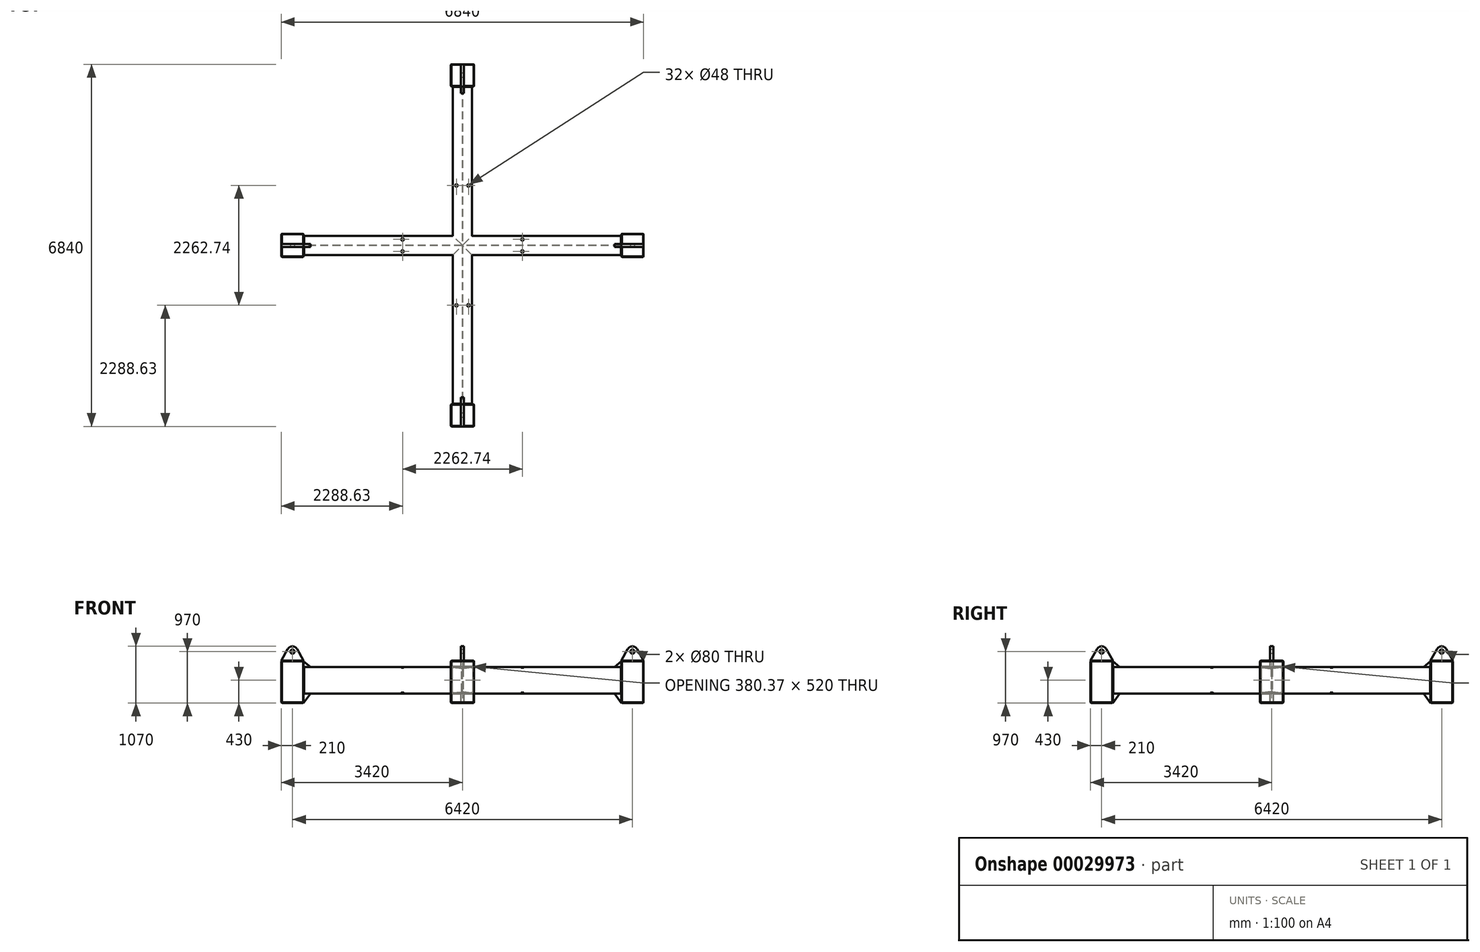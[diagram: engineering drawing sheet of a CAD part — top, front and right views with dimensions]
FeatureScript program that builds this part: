
annotation { "Feature Type Name" : "Feature", "Feature Type Description" : "" }
export const myFeature = defineFeature(function(context is Context, id is Id, definition is map)
    precondition{}
    {
        {
            var Q0;
            Q0=qCreatedBy(makeId("Front.planeOp"),FACE);
            var sketch = newSketch(context, id + "F0", { "sketchPlane" : qUnion([Q0])});
            skLineSegment(sketch, "E0", {"start": v(0, 886.2) * mm, "end": v(0, 0) * mm, "construction": true});
            skLineSegment(sketch, "E1", {"start": v(-180, 0) * mm, "end": v(180, 0) * mm});
            skLineSegment(sketch, "E2", {"start": v(180, 0) * mm, "end": v(180, -5.5) * mm});
            skLineSegment(sketch, "E3", {"start": v(180, -5.5) * mm, "end": v(4.95, -23.9) * mm});
            skLineSegment(sketch, "E4", {"start": v(4.95, -23.9) * mm, "end": v(4.95, -476.1) * mm});
            skLineSegment(sketch, "E5", {"start": v(4.95, -476.1) * mm, "end": v(180, -494.5) * mm});
            skLineSegment(sketch, "E6", {"start": v(180, -494.5) * mm, "end": v(180, -500) * mm});
            skLineSegment(sketch, "E7", {"start": v(180, -500) * mm, "end": v(-180, -500) * mm});
            skLineSegment(sketch, "E8", {"start": v(-180, -500) * mm, "end": v(-180, -494.5) * mm});
            skLineSegment(sketch, "E9", {"start": v(-180, -494.5) * mm, "end": v(-4.95, -476.1) * mm});
            skLineSegment(sketch, "E10", {"start": v(-4.95, -476.1) * mm, "end": v(-4.95, -23.9) * mm});
            skLineSegment(sketch, "E11", {"start": v(-4.95, -23.9) * mm, "end": v(-180, -5.5) * mm});
            skLineSegment(sketch, "E12", {"start": v(-180, -5.5) * mm, "end": v(-180, 0) * mm});
            skLineSegment(sketch, "E13", {"start": v(-180, -5.5) * mm, "end": v(-180, -494.5) * mm, "construction": true});
            skLineSegment(sketch, "E14", {"start": v(180, -5.5) * mm, "end": v(180, -494.5) * mm, "construction": true});
            skLineSegment(sketch, "E15", {"start": v(-4.95, -476.1) * mm, "end": v(4.95, -476.1) * mm, "construction": true});
            skLineSegment(sketch, "E16", {"start": v(-4.95, -23.9) * mm, "end": v(4.95, -23.9) * mm, "construction": true});
            skPoint(sketch, "E17", {"position": v(-92.48, -14.7) * mm});
            skLineSegment(sketch, "E18", {"start": v(-180, -250) * mm, "end": v(-341.33, -250) * mm, "construction": true});
            skSolve(sketch);
        }
        {
            var Q0;
            Q0 = qSketchRegion(id + "F0", true);
            extrude(context, id + "F1", {"entities" : qUnion([Q0]), "endBound" : BoundingType.SYMMETRIC, "depth" : 6000 * mm});
        }
        {
            var Q0;
            Q0=qCreatedBy(makeId("Right.planeOp"),FACE);
            var sketch = newSketch(context, id + "F2", { "sketchPlane" : qUnion([Q0])});
            skLineSegment(sketch, "E19", {"start": v(-180, -250) * mm, "end": v(-341.33, -250) * mm, "construction": true});
            skPoint(sketch, "E20", {"position": v(-92.47, -14.7) * mm});
            skLineSegment(sketch, "E21", {"start": v(-180, -5.5) * mm, "end": v(-180, -494.5) * mm, "construction": true});
            skLineSegment(sketch, "E22", {"start": v(180, -5.5) * mm, "end": v(180, -494.5) * mm, "construction": true});
            skLineSegment(sketch, "E23", {"start": v(0, 648.37) * mm, "end": v(0, -237.84) * mm, "construction": true});
            skLineSegment(sketch, "E24", {"start": v(-180, 0) * mm, "end": v(180, 0) * mm});
            skLineSegment(sketch, "E25", {"start": v(180, -500) * mm, "end": v(-180, -500) * mm});
            skLineSegment(sketch, "E26", {"start": v(180, -5.5) * mm, "end": v(4.95, -23.9) * mm});
            skLineSegment(sketch, "E27", {"start": v(4.95, -23.9) * mm, "end": v(4.95, -476.1) * mm});
            skLineSegment(sketch, "E28", {"start": v(-180, -494.5) * mm, "end": v(-4.95, -476.1) * mm});
            skLineSegment(sketch, "E29", {"start": v(4.95, -476.1) * mm, "end": v(180, -494.5) * mm});
            skLineSegment(sketch, "E30", {"start": v(-4.95, -476.1) * mm, "end": v(-4.95, -23.9) * mm});
            skLineSegment(sketch, "E31", {"start": v(-4.95, -23.9) * mm, "end": v(-180, -5.5) * mm});
            skLineSegment(sketch, "E32", {"start": v(-4.95, -476.1) * mm, "end": v(4.95, -476.1) * mm, "construction": true});
            skLineSegment(sketch, "E33", {"start": v(180, 0) * mm, "end": v(180, -5.5) * mm});
            skLineSegment(sketch, "E34", {"start": v(-180, -500) * mm, "end": v(-180, -494.5) * mm});
            skLineSegment(sketch, "E35", {"start": v(180, -494.5) * mm, "end": v(180, -500) * mm});
            skLineSegment(sketch, "E36", {"start": v(-180, -5.5) * mm, "end": v(-180, 0) * mm});
            skLineSegment(sketch, "E37", {"start": v(-4.95, -23.9) * mm, "end": v(4.95, -23.9) * mm, "construction": true});
            skLineSegment(sketch, "E38", {"start": v(0, 0) * mm, "end": v(0, 2027.1) * mm, "construction": true});
            skSolve(sketch);
        }
        {
            var Q0;
            Q0 = qSketchRegion(id + "F2", true);
            extrude(context, id + "F3", {"entities" : qUnion([Q0]), "operationType" : NewBodyOperationType.ADD, "endBound" : BoundingType.SYMMETRIC, "depth" : 6000 * mm});
        }
        {
            var Q0;
            {var subQ0=sQuery(id+"F0.wireOp",EDGE,"E4");var subQ1=sQuery(id+"F0.wireOp",EDGE,"E5");Q0=makeQuery(id+"F3.boolean.opBoolean","SPLIT",EDGE,{"disambiguationData":[TD([makeQuery(id+"F3.opExtrude","SWEPT_FACE",FACE,{"disambiguationData":[OSD([sQuery(id+"F2.wireOp",EDGE,"E28")])]})])],"derivedFrom":makeQuery(id+"F1.opExtrude","SWEPT_EDGE",EDGE,{"disambiguationData":[OSD([subQ0,subQ1])]})});}
            var Q1;
            {var subQ0=sQuery(id+"F0.wireOp",EDGE,"E9");var subQ1=sQuery(id+"F0.wireOp",EDGE,"E10");Q1=makeQuery(id+"F3.boolean.opBoolean","SPLIT",EDGE,{"disambiguationData":[TD([makeQuery(id+"F3.opExtrude","SWEPT_FACE",FACE,{"disambiguationData":[OSD([sQuery(id+"F2.wireOp",EDGE,"E28")])]})])],"derivedFrom":makeQuery(id+"F1.opExtrude","SWEPT_EDGE",EDGE,{"disambiguationData":[OSD([subQ0,subQ1])]})});}
            var Q2;
            {var subQ0=sQuery(id+"F0.wireOp",EDGE,"E10");var subQ1=sQuery(id+"F0.wireOp",EDGE,"E11");Q2=makeQuery(id+"F3.boolean.opBoolean","SPLIT",EDGE,{"disambiguationData":[TD([makeQuery(id+"F3.opExtrude","SWEPT_FACE",FACE,{"disambiguationData":[OSD([sQuery(id+"F2.wireOp",EDGE,"E30")])]})])],"derivedFrom":makeQuery(id+"F1.opExtrude","SWEPT_EDGE",EDGE,{"disambiguationData":[OSD([subQ0,subQ1])]})});}
            var Q3;
            {var subQ0=sQuery(id+"F0.wireOp",EDGE,"E3");var subQ1=sQuery(id+"F0.wireOp",EDGE,"E4");Q3=makeQuery(id+"F3.boolean.opBoolean","SPLIT",EDGE,{"disambiguationData":[TD([makeQuery(id+"F3.opExtrude","SWEPT_FACE",FACE,{"disambiguationData":[OSD([sQuery(id+"F2.wireOp",EDGE,"E30")])]})])],"derivedFrom":makeQuery(id+"F1.opExtrude","SWEPT_EDGE",EDGE,{"disambiguationData":[OSD([subQ0,subQ1])]})});}
            var Q4;
            {var subQ0=sQuery(id+"F2.wireOp",EDGE,"E30");var subQ1=sQuery(id+"F2.wireOp",EDGE,"E31");Q4=makeQuery(id+"F3.boolean.opBoolean","SPLIT",EDGE,{"disambiguationData":[TD([makeQuery(id+"F1.opExtrude","SWEPT_FACE",FACE,{"disambiguationData":[OSD([sQuery(id+"F0.wireOp",EDGE,"E3")])]})])],"derivedFrom":makeQuery(id+"F3.opExtrude","SWEPT_EDGE",EDGE,{"disambiguationData":[OSD([subQ0,subQ1])]})});}
            var Q5;
            {var subQ0=sQuery(id+"F2.wireOp",EDGE,"E28");var subQ1=sQuery(id+"F2.wireOp",EDGE,"E30");Q5=makeQuery(id+"F3.boolean.opBoolean","SPLIT",EDGE,{"disambiguationData":[TD([makeQuery(id+"F1.opExtrude","SWEPT_FACE",FACE,{"disambiguationData":[OSD([sQuery(id+"F0.wireOp",EDGE,"E4")])]})])],"derivedFrom":makeQuery(id+"F3.opExtrude","SWEPT_EDGE",EDGE,{"disambiguationData":[OSD([subQ0,subQ1])]})});}
            var Q6;
            {var subQ0=sQuery(id+"F2.wireOp",EDGE,"E27");var subQ1=sQuery(id+"F2.wireOp",EDGE,"E29");Q6=makeQuery(id+"F3.boolean.opBoolean","SPLIT",EDGE,{"disambiguationData":[TD([makeQuery(id+"F1.opExtrude","SWEPT_FACE",FACE,{"disambiguationData":[OSD([sQuery(id+"F0.wireOp",EDGE,"E4")])]})])],"derivedFrom":makeQuery(id+"F3.opExtrude","SWEPT_EDGE",EDGE,{"disambiguationData":[OSD([subQ0,subQ1])]})});}
            var Q7;
            {var subQ0=sQuery(id+"F2.wireOp",EDGE,"E26");var subQ1=sQuery(id+"F2.wireOp",EDGE,"E27");Q7=makeQuery(id+"F3.boolean.opBoolean","SPLIT",EDGE,{"disambiguationData":[TD([makeQuery(id+"F1.opExtrude","SWEPT_FACE",FACE,{"disambiguationData":[OSD([sQuery(id+"F0.wireOp",EDGE,"E3")])]})])],"derivedFrom":makeQuery(id+"F3.opExtrude","SWEPT_EDGE",EDGE,{"disambiguationData":[OSD([subQ0,subQ1])]})});}
            var Q8;
            {var subQ0=sQuery(id+"F0.wireOp",EDGE,"E4");var subQ1=sQuery(id+"F0.wireOp",EDGE,"E5");Q8=makeQuery(id+"F3.boolean.opBoolean","SPLIT",EDGE,{"disambiguationData":[TD([makeQuery(id+"F3.opExtrude","SWEPT_FACE",FACE,{"disambiguationData":[OSD([sQuery(id+"F2.wireOp",EDGE,"E27")])]})])],"derivedFrom":makeQuery(id+"F1.opExtrude","SWEPT_EDGE",EDGE,{"disambiguationData":[OSD([subQ0,subQ1])]})});}
            var Q9;
            {var subQ0=sQuery(id+"F0.wireOp",EDGE,"E3");var subQ1=sQuery(id+"F0.wireOp",EDGE,"E4");Q9=makeQuery(id+"F3.boolean.opBoolean","SPLIT",EDGE,{"disambiguationData":[TD([makeQuery(id+"F3.opExtrude","SWEPT_FACE",FACE,{"disambiguationData":[OSD([sQuery(id+"F2.wireOp",EDGE,"E26")])]})])],"derivedFrom":makeQuery(id+"F1.opExtrude","SWEPT_EDGE",EDGE,{"disambiguationData":[OSD([subQ0,subQ1])]})});}
            var Q10;
            {var subQ0=sQuery(id+"F0.wireOp",EDGE,"E9");var subQ1=sQuery(id+"F0.wireOp",EDGE,"E10");Q10=makeQuery(id+"F3.boolean.opBoolean","SPLIT",EDGE,{"disambiguationData":[TD([makeQuery(id+"F3.opExtrude","SWEPT_FACE",FACE,{"disambiguationData":[OSD([sQuery(id+"F2.wireOp",EDGE,"E27")])]})])],"derivedFrom":makeQuery(id+"F1.opExtrude","SWEPT_EDGE",EDGE,{"disambiguationData":[OSD([subQ0,subQ1])]})});}
            var Q11;
            {var subQ0=sQuery(id+"F0.wireOp",EDGE,"E10");var subQ1=sQuery(id+"F0.wireOp",EDGE,"E11");Q11=makeQuery(id+"F3.boolean.opBoolean","SPLIT",EDGE,{"disambiguationData":[TD([makeQuery(id+"F3.opExtrude","SWEPT_FACE",FACE,{"disambiguationData":[OSD([sQuery(id+"F2.wireOp",EDGE,"E26")])]})])],"derivedFrom":makeQuery(id+"F1.opExtrude","SWEPT_EDGE",EDGE,{"disambiguationData":[OSD([subQ0,subQ1])]})});}
            var Q12;
            {var subQ0=sQuery(id+"F2.wireOp",EDGE,"E27");var subQ1=sQuery(id+"F2.wireOp",EDGE,"E29");Q12=makeQuery(id+"F3.boolean.opBoolean","SPLIT",EDGE,{"disambiguationData":[TD([makeQuery(id+"F1.opExtrude","SWEPT_FACE",FACE,{"disambiguationData":[OSD([sQuery(id+"F0.wireOp",EDGE,"E9")])]})])],"derivedFrom":makeQuery(id+"F3.opExtrude","SWEPT_EDGE",EDGE,{"disambiguationData":[OSD([subQ0,subQ1])]})});}
            var Q13;
            {var subQ0=sQuery(id+"F2.wireOp",EDGE,"E26");var subQ1=sQuery(id+"F2.wireOp",EDGE,"E27");Q13=makeQuery(id+"F3.boolean.opBoolean","SPLIT",EDGE,{"disambiguationData":[TD([makeQuery(id+"F1.opExtrude","SWEPT_FACE",FACE,{"disambiguationData":[OSD([sQuery(id+"F0.wireOp",EDGE,"E10")])]})])],"derivedFrom":makeQuery(id+"F3.opExtrude","SWEPT_EDGE",EDGE,{"disambiguationData":[OSD([subQ0,subQ1])]})});}
            var Q14;
            {var subQ0=sQuery(id+"F2.wireOp",EDGE,"E28");var subQ1=sQuery(id+"F2.wireOp",EDGE,"E30");Q14=makeQuery(id+"F3.boolean.opBoolean","SPLIT",EDGE,{"disambiguationData":[TD([makeQuery(id+"F1.opExtrude","SWEPT_FACE",FACE,{"disambiguationData":[OSD([sQuery(id+"F0.wireOp",EDGE,"E9")])]})])],"derivedFrom":makeQuery(id+"F3.opExtrude","SWEPT_EDGE",EDGE,{"disambiguationData":[OSD([subQ0,subQ1])]})});}
            var Q15;
            {var subQ0=sQuery(id+"F2.wireOp",EDGE,"E30");var subQ1=sQuery(id+"F2.wireOp",EDGE,"E31");Q15=makeQuery(id+"F3.boolean.opBoolean","SPLIT",EDGE,{"disambiguationData":[TD([makeQuery(id+"F1.opExtrude","SWEPT_FACE",FACE,{"disambiguationData":[OSD([sQuery(id+"F0.wireOp",EDGE,"E10")])]})])],"derivedFrom":makeQuery(id+"F3.opExtrude","SWEPT_EDGE",EDGE,{"disambiguationData":[OSD([subQ0,subQ1])]})});}
            fillet(context, id + "F4", {"entities" : qUnion([Q0, Q1, Q2, Q3, Q4, Q5, Q6, Q7, Q8, Q9, Q10, Q11, Q12, Q13, Q14, Q15]), "radius" : 16 * mm, "tangentPropagation" : true, "allowEdgeOverflow" : false});
        }
        {
            var Q0;
            {var subQ0=sQuery(id+"F0.wireOp",EDGE,"E5");var subQ1=sQuery(id+"F0.wireOp",EDGE,"E6");Q0=makeQuery(id+"F3.boolean.opBoolean","SPLIT",EDGE,{"disambiguationData":[TD([makeQuery(id+"F3.opExtrude","SWEPT_FACE",FACE,{"disambiguationData":[OSD([sQuery(id+"F2.wireOp",EDGE,"E28")])]})])],"derivedFrom":makeQuery(id+"F1.opExtrude","SWEPT_EDGE",EDGE,{"disambiguationData":[OSD([subQ0,subQ1])]})});}
            var Q1;
            {var subQ0=sQuery(id+"F0.wireOp",EDGE,"E2");var subQ1=sQuery(id+"F0.wireOp",EDGE,"E3");Q1=makeQuery(id+"F3.boolean.opBoolean","SPLIT",EDGE,{"disambiguationData":[TD([makeQuery(id+"F3.opExtrude","SWEPT_FACE",FACE,{"disambiguationData":[OSD([sQuery(id+"F2.wireOp",EDGE,"E31")])]})])],"derivedFrom":makeQuery(id+"F1.opExtrude","SWEPT_EDGE",EDGE,{"disambiguationData":[OSD([subQ0,subQ1])]})});}
            var Q2;
            {var subQ0=sQuery(id+"F0.wireOp",EDGE,"E8");var subQ1=sQuery(id+"F0.wireOp",EDGE,"E9");Q2=makeQuery(id+"F3.boolean.opBoolean","SPLIT",EDGE,{"disambiguationData":[TD([makeQuery(id+"F3.opExtrude","SWEPT_FACE",FACE,{"disambiguationData":[OSD([sQuery(id+"F2.wireOp",EDGE,"E28")])]})])],"derivedFrom":makeQuery(id+"F1.opExtrude","SWEPT_EDGE",EDGE,{"disambiguationData":[OSD([subQ0,subQ1])]})});}
            var Q3;
            {var subQ0=sQuery(id+"F0.wireOp",EDGE,"E11");var subQ1=sQuery(id+"F0.wireOp",EDGE,"E12");Q3=makeQuery(id+"F3.boolean.opBoolean","SPLIT",EDGE,{"disambiguationData":[TD([makeQuery(id+"F3.opExtrude","SWEPT_FACE",FACE,{"disambiguationData":[OSD([sQuery(id+"F2.wireOp",EDGE,"E31")])]})])],"derivedFrom":makeQuery(id+"F1.opExtrude","SWEPT_EDGE",EDGE,{"disambiguationData":[OSD([subQ0,subQ1])]})});}
            var Q4;
            {var subQ0=sQuery(id+"F2.wireOp",EDGE,"E28");var subQ1=sQuery(id+"F2.wireOp",EDGE,"E34");Q4=makeQuery(id+"F3.boolean.opBoolean","SPLIT",EDGE,{"disambiguationData":[TD([makeQuery(id+"F1.opExtrude","SWEPT_FACE",FACE,{"disambiguationData":[OSD([sQuery(id+"F0.wireOp",EDGE,"E8")])]})])],"derivedFrom":makeQuery(id+"F3.opExtrude","SWEPT_EDGE",EDGE,{"disambiguationData":[OSD([subQ0,subQ1])]})});}
            var Q5;
            {var subQ0=sQuery(id+"F2.wireOp",EDGE,"E31");var subQ1=sQuery(id+"F2.wireOp",EDGE,"E36");Q5=makeQuery(id+"F3.boolean.opBoolean","SPLIT",EDGE,{"disambiguationData":[TD([makeQuery(id+"F1.opExtrude","SWEPT_FACE",FACE,{"disambiguationData":[OSD([sQuery(id+"F0.wireOp",EDGE,"E11")])]})])],"derivedFrom":makeQuery(id+"F3.opExtrude","SWEPT_EDGE",EDGE,{"disambiguationData":[OSD([subQ0,subQ1])]})});}
            var Q6;
            {var subQ0=sQuery(id+"F2.wireOp",EDGE,"E28");var subQ1=sQuery(id+"F2.wireOp",EDGE,"E34");Q6=makeQuery(id+"F3.boolean.opBoolean","SPLIT",EDGE,{"disambiguationData":[TD([makeQuery(id+"F1.opExtrude","SWEPT_FACE",FACE,{"disambiguationData":[OSD([sQuery(id+"F0.wireOp",EDGE,"E5")])]})])],"derivedFrom":makeQuery(id+"F3.opExtrude","SWEPT_EDGE",EDGE,{"disambiguationData":[OSD([subQ0,subQ1])]})});}
            var Q7;
            {var subQ0=sQuery(id+"F2.wireOp",EDGE,"E31");var subQ1=sQuery(id+"F2.wireOp",EDGE,"E36");Q7=makeQuery(id+"F3.boolean.opBoolean","SPLIT",EDGE,{"disambiguationData":[TD([makeQuery(id+"F1.opExtrude","SWEPT_FACE",FACE,{"disambiguationData":[OSD([sQuery(id+"F0.wireOp",EDGE,"E2")])]})])],"derivedFrom":makeQuery(id+"F3.opExtrude","SWEPT_EDGE",EDGE,{"disambiguationData":[OSD([subQ0,subQ1])]})});}
            var Q8;
            {var subQ0=sQuery(id+"F2.wireOp",EDGE,"E29");var subQ1=sQuery(id+"F2.wireOp",EDGE,"E35");Q8=makeQuery(id+"F3.boolean.opBoolean","SPLIT",EDGE,{"disambiguationData":[TD([makeQuery(id+"F1.opExtrude","SWEPT_FACE",FACE,{"disambiguationData":[OSD([sQuery(id+"F0.wireOp",EDGE,"E5")])]})])],"derivedFrom":makeQuery(id+"F3.opExtrude","SWEPT_EDGE",EDGE,{"disambiguationData":[OSD([subQ0,subQ1])]})});}
            var Q9;
            {var subQ0=sQuery(id+"F2.wireOp",EDGE,"E26");var subQ1=sQuery(id+"F2.wireOp",EDGE,"E33");Q9=makeQuery(id+"F3.boolean.opBoolean","SPLIT",EDGE,{"disambiguationData":[TD([makeQuery(id+"F1.opExtrude","SWEPT_FACE",FACE,{"disambiguationData":[OSD([sQuery(id+"F0.wireOp",EDGE,"E2")])]})])],"derivedFrom":makeQuery(id+"F3.opExtrude","SWEPT_EDGE",EDGE,{"disambiguationData":[OSD([subQ0,subQ1])]})});}
            var Q10;
            {var subQ0=sQuery(id+"F0.wireOp",EDGE,"E2");var subQ1=sQuery(id+"F0.wireOp",EDGE,"E3");Q10=makeQuery(id+"F3.boolean.opBoolean","SPLIT",EDGE,{"disambiguationData":[TD([makeQuery(id+"F3.opExtrude","SWEPT_FACE",FACE,{"disambiguationData":[OSD([sQuery(id+"F2.wireOp",EDGE,"E26")])]})])],"derivedFrom":makeQuery(id+"F1.opExtrude","SWEPT_EDGE",EDGE,{"disambiguationData":[OSD([subQ0,subQ1])]})});}
            var Q11;
            {var subQ0=sQuery(id+"F0.wireOp",EDGE,"E5");var subQ1=sQuery(id+"F0.wireOp",EDGE,"E6");Q11=makeQuery(id+"F3.boolean.opBoolean","SPLIT",EDGE,{"disambiguationData":[TD([makeQuery(id+"F3.opExtrude","SWEPT_FACE",FACE,{"disambiguationData":[OSD([sQuery(id+"F2.wireOp",EDGE,"E29")])]})])],"derivedFrom":makeQuery(id+"F1.opExtrude","SWEPT_EDGE",EDGE,{"disambiguationData":[OSD([subQ0,subQ1])]})});}
            var Q12;
            {var subQ0=sQuery(id+"F0.wireOp",EDGE,"E8");var subQ1=sQuery(id+"F0.wireOp",EDGE,"E9");Q12=makeQuery(id+"F3.boolean.opBoolean","SPLIT",EDGE,{"disambiguationData":[TD([makeQuery(id+"F3.opExtrude","SWEPT_FACE",FACE,{"disambiguationData":[OSD([sQuery(id+"F2.wireOp",EDGE,"E29")])]})])],"derivedFrom":makeQuery(id+"F1.opExtrude","SWEPT_EDGE",EDGE,{"disambiguationData":[OSD([subQ0,subQ1])]})});}
            var Q13;
            {var subQ0=sQuery(id+"F0.wireOp",EDGE,"E11");var subQ1=sQuery(id+"F0.wireOp",EDGE,"E12");Q13=makeQuery(id+"F3.boolean.opBoolean","SPLIT",EDGE,{"disambiguationData":[TD([makeQuery(id+"F3.opExtrude","SWEPT_FACE",FACE,{"disambiguationData":[OSD([sQuery(id+"F2.wireOp",EDGE,"E26")])]})])],"derivedFrom":makeQuery(id+"F1.opExtrude","SWEPT_EDGE",EDGE,{"disambiguationData":[OSD([subQ0,subQ1])]})});}
            var Q14;
            {var subQ0=sQuery(id+"F2.wireOp",EDGE,"E26");var subQ1=sQuery(id+"F2.wireOp",EDGE,"E33");Q14=makeQuery(id+"F3.boolean.opBoolean","SPLIT",EDGE,{"disambiguationData":[TD([makeQuery(id+"F1.opExtrude","SWEPT_FACE",FACE,{"disambiguationData":[OSD([sQuery(id+"F0.wireOp",EDGE,"E11")])]})])],"derivedFrom":makeQuery(id+"F3.opExtrude","SWEPT_EDGE",EDGE,{"disambiguationData":[OSD([subQ0,subQ1])]})});}
            var Q15;
            {var subQ0=sQuery(id+"F2.wireOp",EDGE,"E29");var subQ1=sQuery(id+"F2.wireOp",EDGE,"E35");Q15=makeQuery(id+"F3.boolean.opBoolean","SPLIT",EDGE,{"disambiguationData":[TD([makeQuery(id+"F1.opExtrude","SWEPT_FACE",FACE,{"disambiguationData":[OSD([sQuery(id+"F0.wireOp",EDGE,"E8")])]})])],"derivedFrom":makeQuery(id+"F3.opExtrude","SWEPT_EDGE",EDGE,{"disambiguationData":[OSD([subQ0,subQ1])]})});}
            fillet(context, id + "F5", {"entities" : qUnion([Q0, Q1, Q2, Q3, Q4, Q5, Q6, Q7, Q8, Q9, Q10, Q11, Q12, Q13, Q14, Q15]), "radius" : 8 * mm, "tangentPropagation" : true, "allowEdgeOverflow" : false});
        }
        {
            var Q0;
            Q0=makeQuery(id+"F3.boolean.opBoolean","MERGE",FACE,{"derivedFrom":[makeQuery(id+"F1.opExtrude","SWEPT_FACE",FACE,{"disambiguationData":[OSD([sQuery(id+"F0.wireOp",EDGE,"E1")])]}),makeQuery(id+"F3.opExtrude","SWEPT_FACE",FACE,{"disambiguationData":[OSD([sQuery(id+"F2.wireOp",EDGE,"E24")])]})]});
            var sketch = newSketch(context, id + "F6", { "sketchPlane" : qUnion([Q0])});
            skLineSegment(sketch, "E39", {"start": v(0, 0) * mm, "end": v(4594.2, 0) * mm, "construction": true});
            skLineSegment(sketch, "E40.bottom", {"start": v(3000, 220) * mm, "end": v(3420, 220) * mm});
            skLineSegment(sketch, "E40.top", {"start": v(3000, -220) * mm, "end": v(3420, -220) * mm});
            skLineSegment(sketch, "E40.left", {"start": v(3000, 220) * mm, "end": v(3000, -220) * mm});
            skLineSegment(sketch, "E40.right", {"start": v(3420, 220) * mm, "end": v(3420, -220) * mm});
            skLineSegment(sketch, "E41", {"start": v(0, 0) * mm, "end": v(0, 3976.5) * mm, "construction": true});
            skLineSegment(sketch, "E42.MirrorCS", {"start": v(-3000, -220) * mm, "end": v(-3420, -220) * mm});
            skLineSegment(sketch, "E43.MirrorCS", {"start": v(-3420, 220) * mm, "end": v(-3420, -220) * mm});
            skLineSegment(sketch, "E44.MirrorCS", {"start": v(-3000, 220) * mm, "end": v(-3000, -220) * mm});
            skLineSegment(sketch, "E45.MirrorCS", {"start": v(-3000, 220) * mm, "end": v(-3420, 220) * mm});
            skLineSegment(sketch, "E46.bottom", {"start": v(-220, 3420) * mm, "end": v(220, 3420) * mm});
            skLineSegment(sketch, "E46.top", {"start": v(-220, 3000) * mm, "end": v(220, 3000) * mm});
            skLineSegment(sketch, "E46.left", {"start": v(-220, 3420) * mm, "end": v(-220, 3000) * mm});
            skLineSegment(sketch, "E46.right", {"start": v(220, 3420) * mm, "end": v(220, 3000) * mm});
            skLineSegment(sketch, "E47.MirrorCS", {"start": v(220, -3420) * mm, "end": v(220, -3000) * mm});
            skLineSegment(sketch, "E48.MirrorCS", {"start": v(-220, -3420) * mm, "end": v(220, -3420) * mm});
            skLineSegment(sketch, "E49.MirrorCS", {"start": v(-220, -3000) * mm, "end": v(220, -3000) * mm});
            skLineSegment(sketch, "E50.MirrorCS", {"start": v(-220, -3420) * mm, "end": v(-220, -3000) * mm});
            skSolve(sketch);
        }
        {
            var Q0;
            Q0 = qSketchRegion(id + "F6", true);
            extrude(context, id + "F7", {"entities" : qUnion([Q0]), "operationType" : NewBodyOperationType.ADD, "depth" : 120 * mm, "hasSecondDirection" : true, "secondDirectionOppositeDirection" : true, "secondDirectionDepth" : (800 - 120) * mm});
        }
        {
            var Q0;
            Q0=makeQuery(id+"F7.opExtrude","SWEPT_FACE",FACE,{"disambiguationData":[OSD([sQuery(id+"F6.wireOp",EDGE,"E40.top")])]});
            var Q1;
            Q1=makeQuery(id+"F7.opExtrude","SWEPT_FACE",FACE,{"disambiguationData":[OSD([sQuery(id+"F6.wireOp",EDGE,"E40.right")])]});
            var Q2;
            Q2=makeQuery(id+"F7.opExtrude","CAP_FACE",FACE,{"disambiguationData":[OSD([sQuery(id+"F6.wireOp",EDGE,"E40.bottom"),sQuery(id+"F6.wireOp",EDGE,"E40.top"),sQuery(id+"F6.wireOp",EDGE,"E40.left"),sQuery(id+"F6.wireOp",EDGE,"E40.right")])],"isStart":false});
            var Q3;
            Q3=makeQuery(id+"F7.opExtrude","SWEPT_FACE",FACE,{"disambiguationData":[OSD([sQuery(id+"F6.wireOp",EDGE,"E40.bottom")])]});
            var Q4;
            Q4=makeQuery(id+"F7.opExtrude","CAP_FACE",FACE,{"disambiguationData":[OSD([sQuery(id+"F6.wireOp",EDGE,"E40.bottom"),sQuery(id+"F6.wireOp",EDGE,"E40.top"),sQuery(id+"F6.wireOp",EDGE,"E40.left"),sQuery(id+"F6.wireOp",EDGE,"E40.right")])],"isStart":true});
            var Q5;
            Q5=makeQuery(id+"F7.opExtrude","SWEPT_FACE",FACE,{"disambiguationData":[OSD([sQuery(id+"F6.wireOp",EDGE,"E40.left")])]});
            var Q6;
            Q6=makeQuery(id+"F7.opExtrude","SWEPT_FACE",FACE,{"disambiguationData":[OSD([sQuery(id+"F6.wireOp",EDGE,"E48.MirrorCS")])]});
            var Q7;
            Q7=makeQuery(id+"F7.opExtrude","SWEPT_FACE",FACE,{"disambiguationData":[OSD([sQuery(id+"F6.wireOp",EDGE,"E47.MirrorCS")])]});
            var Q8;
            Q8=makeQuery(id+"F7.opExtrude","CAP_FACE",FACE,{"disambiguationData":[OSD([sQuery(id+"F6.wireOp",EDGE,"E47.MirrorCS"),sQuery(id+"F6.wireOp",EDGE,"E48.MirrorCS"),sQuery(id+"F6.wireOp",EDGE,"E49.MirrorCS"),sQuery(id+"F6.wireOp",EDGE,"E50.MirrorCS")])],"isStart":false});
            var Q9;
            Q9=makeQuery(id+"F7.opExtrude","SWEPT_FACE",FACE,{"disambiguationData":[OSD([sQuery(id+"F6.wireOp",EDGE,"E50.MirrorCS")])]});
            var Q10;
            Q10=makeQuery(id+"F7.opExtrude","CAP_FACE",FACE,{"disambiguationData":[OSD([sQuery(id+"F6.wireOp",EDGE,"E47.MirrorCS"),sQuery(id+"F6.wireOp",EDGE,"E48.MirrorCS"),sQuery(id+"F6.wireOp",EDGE,"E49.MirrorCS"),sQuery(id+"F6.wireOp",EDGE,"E50.MirrorCS")])],"isStart":true});
            var Q11;
            Q11=makeQuery(id+"F7.opExtrude","SWEPT_FACE",FACE,{"disambiguationData":[OSD([sQuery(id+"F6.wireOp",EDGE,"E49.MirrorCS")])]});
            var Q12;
            Q12=makeQuery(id+"F7.opExtrude","SWEPT_FACE",FACE,{"disambiguationData":[OSD([sQuery(id+"F6.wireOp",EDGE,"E45.MirrorCS")])]});
            var Q13;
            Q13=makeQuery(id+"F7.opExtrude","CAP_FACE",FACE,{"disambiguationData":[OSD([sQuery(id+"F6.wireOp",EDGE,"E42.MirrorCS"),sQuery(id+"F6.wireOp",EDGE,"E43.MirrorCS"),sQuery(id+"F6.wireOp",EDGE,"E44.MirrorCS"),sQuery(id+"F6.wireOp",EDGE,"E45.MirrorCS")])],"isStart":true});
            var Q14;
            Q14=makeQuery(id+"F7.opExtrude","SWEPT_FACE",FACE,{"disambiguationData":[OSD([sQuery(id+"F6.wireOp",EDGE,"E43.MirrorCS")])]});
            var Q15;
            Q15=makeQuery(id+"F7.opExtrude","SWEPT_FACE",FACE,{"disambiguationData":[OSD([sQuery(id+"F6.wireOp",EDGE,"E42.MirrorCS")])]});
            var Q16;
            Q16=makeQuery(id+"F7.opExtrude","CAP_FACE",FACE,{"disambiguationData":[OSD([sQuery(id+"F6.wireOp",EDGE,"E42.MirrorCS"),sQuery(id+"F6.wireOp",EDGE,"E43.MirrorCS"),sQuery(id+"F6.wireOp",EDGE,"E44.MirrorCS"),sQuery(id+"F6.wireOp",EDGE,"E45.MirrorCS")])],"isStart":false});
            var Q17;
            Q17=makeQuery(id+"F7.opExtrude","SWEPT_FACE",FACE,{"disambiguationData":[OSD([sQuery(id+"F6.wireOp",EDGE,"E44.MirrorCS")])]});
            var Q18;
            Q18=makeQuery(id+"F7.opExtrude","SWEPT_FACE",FACE,{"disambiguationData":[OSD([sQuery(id+"F6.wireOp",EDGE,"E46.left")])]});
            var Q19;
            Q19=makeQuery(id+"F7.opExtrude","SWEPT_FACE",FACE,{"disambiguationData":[OSD([sQuery(id+"F6.wireOp",EDGE,"E46.top")])]});
            var Q20;
            Q20=makeQuery(id+"F7.opExtrude","CAP_FACE",FACE,{"disambiguationData":[OSD([sQuery(id+"F6.wireOp",EDGE,"E46.bottom"),sQuery(id+"F6.wireOp",EDGE,"E46.top"),sQuery(id+"F6.wireOp",EDGE,"E46.left"),sQuery(id+"F6.wireOp",EDGE,"E46.right")])],"isStart":false});
            var Q21;
            Q21=makeQuery(id+"F7.opExtrude","SWEPT_FACE",FACE,{"disambiguationData":[OSD([sQuery(id+"F6.wireOp",EDGE,"E46.bottom")])]});
            var Q22;
            Q22=makeQuery(id+"F7.opExtrude","SWEPT_FACE",FACE,{"disambiguationData":[OSD([sQuery(id+"F6.wireOp",EDGE,"E46.right")])]});
            var Q23;
            Q23=makeQuery(id+"F7.opExtrude","CAP_FACE",FACE,{"disambiguationData":[OSD([sQuery(id+"F6.wireOp",EDGE,"E46.bottom"),sQuery(id+"F6.wireOp",EDGE,"E46.top"),sQuery(id+"F6.wireOp",EDGE,"E46.left"),sQuery(id+"F6.wireOp",EDGE,"E46.right")])],"isStart":true});
            chamfer(context, id + "F8", {"entities" : qUnion([Q0, Q1, Q2, Q3, Q4, Q5, Q6, Q7, Q8, Q9, Q10, Q11, Q12, Q13, Q14, Q15, Q16, Q17, Q18, Q19, Q20, Q21, Q22, Q23]), "width" : 10 * mm, "tangentPropagation" : true});
        }
        {
            var Q0;
            Q0=qCreatedBy(makeId("Right.planeOp"),FACE);
            var sketch = newSketch(context, id + "F9", { "sketchPlane" : qUnion([Q0])});
            skLineSegment(sketch, "E51", {"start": v(3000, 120) * mm, "end": v(3420, 120) * mm});
            skLineSegment(sketch, "E52", {"start": v(3210, 120) * mm, "end": v(3210, 538.77) * mm, "construction": true});
            skCircle(sketch, "E53", {"center": v(3210, 290) * mm, "radius": 40 * mm});
            skArc(sketch, "E54", {"start": v(3297.22, 338.92) * mm, "mid": v(3210, 390) * mm, "end": v(3122.78, 338.92) * mm});
            skLineSegment(sketch, "E55", {"start": v(3000, 120) * mm, "end": v(3122.78, 338.92) * mm});
            skLineSegment(sketch, "E56", {"start": v(3420, 120) * mm, "end": v(3297.22, 338.92) * mm});
            skLineSegment(sketch, "E57", {"start": v(2870, 0) * mm, "end": v(3000, 0) * mm});
            skLineSegment(sketch, "E58", {"start": v(2870, -500) * mm, "end": v(3000, -500) * mm});
            skLineSegment(sketch, "E59", {"start": v(3000, -500) * mm, "end": v(3000, -680) * mm});
            skLineSegment(sketch, "E60", {"start": v(3000, -680) * mm, "end": v(2870, -500) * mm});
            skLineSegment(sketch, "E61", {"start": v(2870, -500) * mm, "end": v(2870, 0) * mm, "construction": true});
            skLineSegment(sketch, "E62", {"start": v(2870, 0) * mm, "end": v(3000, 110) * mm});
            skLineSegment(sketch, "E63", {"start": v(3000, 110) * mm, "end": v(3000, 0) * mm});
            skSolve(sketch);
        }
        {
            var Q0;
            Q0=makeQuery(id+"F9.imprint","IMPRINT",FACE,{"disambiguationData":[TD([[makeQuery(id+"F9.imprint","IMPRINT",EDGE,{"derivedFrom":sQuery(id+"F9.wireOp",EDGE,"E58")}),-1.0]])]});
            var Q1;
            Q1=makeQuery(id+"F9.imprint","IMPRINT",FACE,{"disambiguationData":[TD([[makeQuery(id+"F9.imprint","IMPRINT",EDGE,{"derivedFrom":sQuery(id+"F9.wireOp",EDGE,"E57")}),1.0]])]});
            var Q2;
            Q2=makeQuery(id+"F9.imprint","IMPRINT",FACE,{"disambiguationData":[TD([[makeQuery(id+"F9.imprint","IMPRINT",EDGE,{"derivedFrom":sQuery(id+"F9.wireOp",EDGE,"E57")}),1.0]])]});
            var Q3;
            Q3=makeQuery(id+"F9.imprint","IMPRINT",FACE,{"disambiguationData":[TD([[makeQuery(id+"F9.imprint","IMPRINT",EDGE,{"derivedFrom":sQuery(id+"F9.wireOp",EDGE,"E51")}),1.0]])]});
            extrude(context, id + "F10", {"entities" : qUnion([Q0, Q1, Q2, Q3]), "operationType" : NewBodyOperationType.ADD, "endBound" : BoundingType.SYMMETRIC, "depth" : 60 * mm});
        }
        {
            var Q0;
            Q0=makeQuery(id+"F1.opExtrude","SWEPT_BODY",BODY,{"disambiguationData":[OSD([sQuery(id+"F0.wireOp",EDGE,"E1"),sQuery(id+"F0.wireOp",EDGE,"E2"),sQuery(id+"F0.wireOp",EDGE,"E3"),sQuery(id+"F0.wireOp",EDGE,"E4"),sQuery(id+"F0.wireOp",EDGE,"E5"),sQuery(id+"F0.wireOp",EDGE,"E6"),sQuery(id+"F0.wireOp",EDGE,"E7"),sQuery(id+"F0.wireOp",EDGE,"E8"),sQuery(id+"F0.wireOp",EDGE,"E9"),sQuery(id+"F0.wireOp",EDGE,"E10"),sQuery(id+"F0.wireOp",EDGE,"E11"),sQuery(id+"F0.wireOp",EDGE,"E12")])]});
            var Q1;
            Q1=qCreatedBy(makeId("Front.planeOp"),FACE);
            mirror(context, id + "F11", {"operationType" : NewBodyOperationType.ADD, "entities" : qUnion([Q0]), "mirrorPlane" : qUnion([Q1])});
        }
        {
            var Q0;
            Q0=makeQuery(id+"F3.boolean.opBoolean","MERGE",FACE,{"derivedFrom":[makeQuery(id+"F1.opExtrude","SWEPT_FACE",FACE,{"disambiguationData":[OSD([sQuery(id+"F0.wireOp",EDGE,"E1")])]}),makeQuery(id+"F3.opExtrude","SWEPT_FACE",FACE,{"disambiguationData":[OSD([sQuery(id+"F2.wireOp",EDGE,"E24")])]})]});
            var sketch = newSketch(context, id + "F12", { "sketchPlane" : qUnion([Q0])});
            skCircle(sketch, "E64", {"center": v(0, 0) * mm, "radius": 1181.77 * mm, "construction": true});
            skSolve(sketch);
        }
        {
            var Q0;
            Q0=makeQuery(id+"F1.opExtrude","SWEPT_BODY",BODY,{"disambiguationData":[OSD([sQuery(id+"F0.wireOp",EDGE,"E1"),sQuery(id+"F0.wireOp",EDGE,"E2"),sQuery(id+"F0.wireOp",EDGE,"E3"),sQuery(id+"F0.wireOp",EDGE,"E4"),sQuery(id+"F0.wireOp",EDGE,"E5"),sQuery(id+"F0.wireOp",EDGE,"E6"),sQuery(id+"F0.wireOp",EDGE,"E7"),sQuery(id+"F0.wireOp",EDGE,"E8"),sQuery(id+"F0.wireOp",EDGE,"E9"),sQuery(id+"F0.wireOp",EDGE,"E10"),sQuery(id+"F0.wireOp",EDGE,"E11"),sQuery(id+"F0.wireOp",EDGE,"E12")])]});
            var Q1;
            Q1=sQuery(id+"F12.wireOp",EDGE,"E64");
            circularPattern(context, id + "F13", {"entities" : qUnion([Q0]), "axis" : qUnion([Q1]), "angle" : 90 * degree, "instanceCount" : 2});
        }
        {
            var Q0;
            Q0=makeQuery(id+"F3.boolean.opBoolean","MERGE",FACE,{"derivedFrom":[makeQuery(id+"F1.opExtrude","SWEPT_FACE",FACE,{"disambiguationData":[OSD([sQuery(id+"F0.wireOp",EDGE,"E1")])]}),makeQuery(id+"F3.opExtrude","SWEPT_FACE",FACE,{"disambiguationData":[OSD([sQuery(id+"F2.wireOp",EDGE,"E24")])]})]});
            var sketch = newSketch(context, id + "F14", { "sketchPlane" : qUnion([Q0])});
            skLineSegment(sketch, "E65", {"start": v(0, 0) * mm, "end": v(1131.37, 0) * mm, "construction": true});
            skLineSegment(sketch, "E66", {"start": v(0, 0) * mm, "end": v(0, 1131.37) * mm, "construction": true});
            skCircle(sketch, "E67", {"center": v(1131.37, 113.14) * mm, "radius": 24 * mm});
            skCircle(sketch, "E68", {"center": v(1131.37, -113.14) * mm, "radius": 24 * mm});
            skLineSegment(sketch, "E69", {"start": v(1131.37, 113.14) * mm, "end": v(1131.37, -113.14) * mm, "construction": true});
            skLineSegment(sketch, "E70.MirrorCS", {"start": v(2262.74, 0) * mm, "end": v(2262.74, 1131.37) * mm, "construction": true});
            skCircle(sketch, "E71.MirrorC", {"center": v(-1131.37, 113.14) * mm, "radius": 24 * mm});
            skCircle(sketch, "E72.MirrorC", {"center": v(-1131.37, -113.14) * mm, "radius": 24 * mm});
            skCircle(sketch, "E73", {"center": v(-113.14, 1131.37) * mm, "radius": 24 * mm});
            skCircle(sketch, "E74", {"center": v(113.14, 1131.37) * mm, "radius": 24 * mm});
            skLineSegment(sketch, "E75", {"start": v(-113.14, 1131.37) * mm, "end": v(113.14, 1131.37) * mm, "construction": true});
            skCircle(sketch, "E76.MirrorC", {"center": v(-113.14, -1131.37) * mm, "radius": 24 * mm});
            skCircle(sketch, "E77.MirrorC", {"center": v(113.14, -1131.37) * mm, "radius": 24 * mm});
            skSolve(sketch);
        }
        {
            var Q0;
            Q0 = qSketchRegion(id + "F14", true);
            extrude(context, id + "F15", {"entities" : qUnion([Q0]), "operationType" : NewBodyOperationType.REMOVE, "oppositeDirection" : true, "depth" : 500 * mm});
        }
    });
